# Revit family: Скамейка стальная «Simple line» без спинки Арт 12272
name_source: partatom
category: Антураж
revit_build: Autodesk Revit 2018 (Build: 20180423_1000(x64)
units: mm (PartAtom-declared; Revit-internal decimal feet)

## family parameters
Всегда вертикально = Да
Источник визуального образа = Геометрия семейства
На основе рабочей плоскости = Нет
Общий = Нет
При загрузке вырезать с полостями = Нет
Точка расчета площади = Нет

## types (3) — shared parameters
URL = https://hobbyka.ru
Артикул товара = Арт. 12272
Высота = 450 мм
Группа модели = Уличные скамьи
Изготовитель = ООО «Хоббика»
Изображение типоразмера = Скамейка стальная «Simple line» без спинки Арт 12272.jpg
Материал изделия = Сталь, дерево
Цвет лавки = Дерево
Цвет опор = Сталь
Ширина = 430 мм

## per-type parameters (varying)
| type | Версия 1,5 м | Версия 1,8 м | Версия 2,0 м | Длина | Описание |
| Версия 1,5 м | Да | Нет | Нет | 1500 мм | Скамейка стальная «Simple line» без спинки. Версия 1,5 м |
| Версия 1,8 м | Нет | Да | Нет | 1800 мм | Скамейка стальная «Simple line» без спинки. Версия 1,8 м |
| Версия 2,0 м | Нет | Нет | Да | 2000 мм | Скамейка стальная «Simple line» без спинки. Версия 2,0 м |
